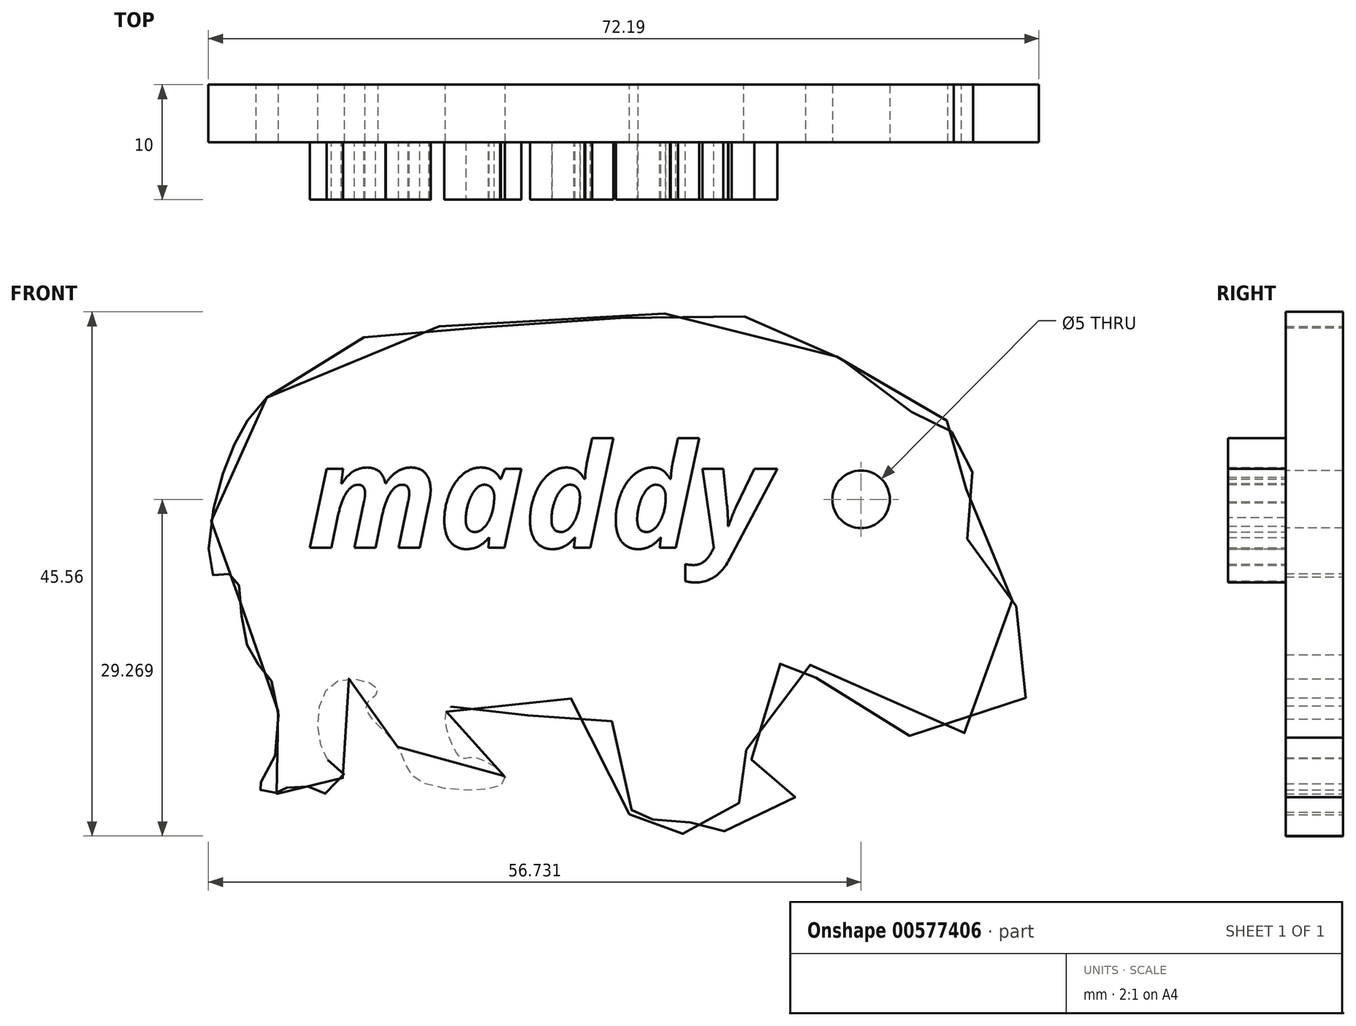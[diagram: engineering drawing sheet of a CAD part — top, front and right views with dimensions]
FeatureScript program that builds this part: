
annotation { "Feature Type Name" : "Feature", "Feature Type Description" : "" }
export const myFeature = defineFeature(function(context is Context, id is Id, definition is map)
    precondition{}
    {
        {
            var Q0;
            Q0=qCreatedBy(makeId("Front.planeOp"),FACE);
            var sketch = newSketch(context, id + "F0", { "sketchPlane" : qUnion([Q0])});
            skFitSpline(sketch, "E0", {"points": [v(-66.89, 38.09) * mm, v(-69.59, 34.26) * mm, v(-71.62, 27.95) * mm, v(-71.4, 22.55) * mm, v(-69.82, 22.77) * mm, v(-69.14, 19.62) * mm, v(-68.01, 15.34) * mm, v(-66.44, 13.32) * mm, v(-66.66, 5.66) * mm, v(-67.79, 4.08) * mm, v(-66.21, 3.86) * mm, v(-65.99, 3.63) * mm, v(-64.18, 4.53) * mm, v(-61.93, 3.63) * mm, v(-61.03, 4.53) * mm, v(-60.13, 5.2) * mm, v(-61.7, 6.78) * mm, v(-61.03, 13.32) * mm, v(-57.2, 12.64) * mm, v(-58.33, 11.29) * mm, v(-55.63, 7.91) * mm, v(-53.6, 4.76) * mm, v(-46.17, 4.76) * mm, v(-48.87, 6.78) * mm, v(-50, 6.78) * mm, v(-51.35, 9.94) * mm, v(-50.67, 11.29) * mm, v(-45.5, 10.16) * mm, v(-38.74, 11.74) * mm, v(-34.68, 2.96) * mm, v(-35.36, 1.83) * mm, v(-33.78, 0) * mm, v(-33.1, 1.83) * mm, v(-31.08, 0) * mm, v(-29.28, 2.06) * mm, v(-27.25, 0) * mm, v(-26.35, 2.5) * mm, v(-20.04, 3.4) * mm, v(-25, 7.01) * mm, v(-22.07, 15.12) * mm, v(-20.04, 15.57) * mm, v(-19.14, 13.77) * mm, v(-10.14, 8.59) * mm, v(0, 13.54) * mm, v(-2.48, 20.97) * mm, v(-5.86, 25.48) * mm, v(-6.3, 29.53) * mm, v(-5.63, 32.46) * mm, v(-7.66, 34.03) * mm, v(-7.2, 35.84) * mm, v(-9.91, 36.29) * mm, v(-11.94, 38.09) * mm, v(-20.04, 43.04) * mm, v(-28.38, 45.52) * mm, v(-44.82, 44.17) * mm, v(-57.2, 43.72) * mm, v(-66.89, 38.09) * mm]});
            skSolve(sketch);
        }
        {
            var Q0;
            Q0=makeQuery(id+"F0.imprint","IMPRINT",FACE,{"disambiguationData":[TD([[makeQuery(id+"F0.imprint","IMPRINT",EDGE,{"derivedFrom":sQuery(id+"F0.wireOp",EDGE,"E0")}),1.0]])]});
            extrude(context, id + "F1", {"entities" : qUnion([Q0]), "depth" : 5 * mm, "offsetDistance" : 25 * mm});
        }
        {
            var Q0;
            Q0=makeQuery(id+"F1.opExtrude","CAP_FACE",FACE,{"disambiguationData":[OSD([sQuery(id+"F0.wireOp",EDGE,"E0")])],"isStart":false});
            var sketch = newSketch(context, id + "F2", { "sketchPlane" : qUnion([Q0])});
            skPoint(sketch, "E1", {"position": v(-15.23, 29.25) * mm});
            skSolve(sketch);
        }
        {
            var Q0;
            Q0=sQuery(id+"F2.wireOp",VERTEX,"E1");
            var Q1;
            Q1=makeQuery(id+"F1.opExtrude","SWEPT_BODY",BODY,{"disambiguationData":[OSD([sQuery(id+"F0.wireOp",EDGE,"E0")])]});
            hole(context, id + "F3", {"style" : HoleStyle.SIMPLE, "endStyle" : HoleEndStyle.THROUGH, "holeDiameter" : 5 * mm, "majorDiameter" : 5 * mm, "isTappedThrough" : true, "tappedDepth" : 12 * mm, "tapClearance" : 3, "locations" : qUnion([Q0]), "scope" : qUnion([Q1])});
        }
        {
            var Q0;
            Q0=makeQuery(id+"F1.opExtrude","CAP_FACE",FACE,{"disambiguationData":[OSD([sQuery(id+"F0.wireOp",EDGE,"E0")])],"isStart":false});
            var sketch = newSketch(context, id + "F4", { "sketchPlane" : qUnion([Q0])});
            skText(sketch, "E2", { "text": "maddy", "fontName": "OpenSans-BoldItalic.ttf"});
            const initialGuessF4  = {"E2": [-0.06336, 0.02504, 1, 0, 0.00903]};
            skSetInitialGuess(sketch, initialGuessF4);
            skSolve(sketch);
        }
        {
            var Q0;
            Q0 = qSketchRegion(id + "F4", true);
            extrude(context, id + "F5", {"entities" : qUnion([Q0]), "operationType" : NewBodyOperationType.ADD, "depth" : 5 * mm, "offsetDistance" : 25 * mm});
        }
    });
